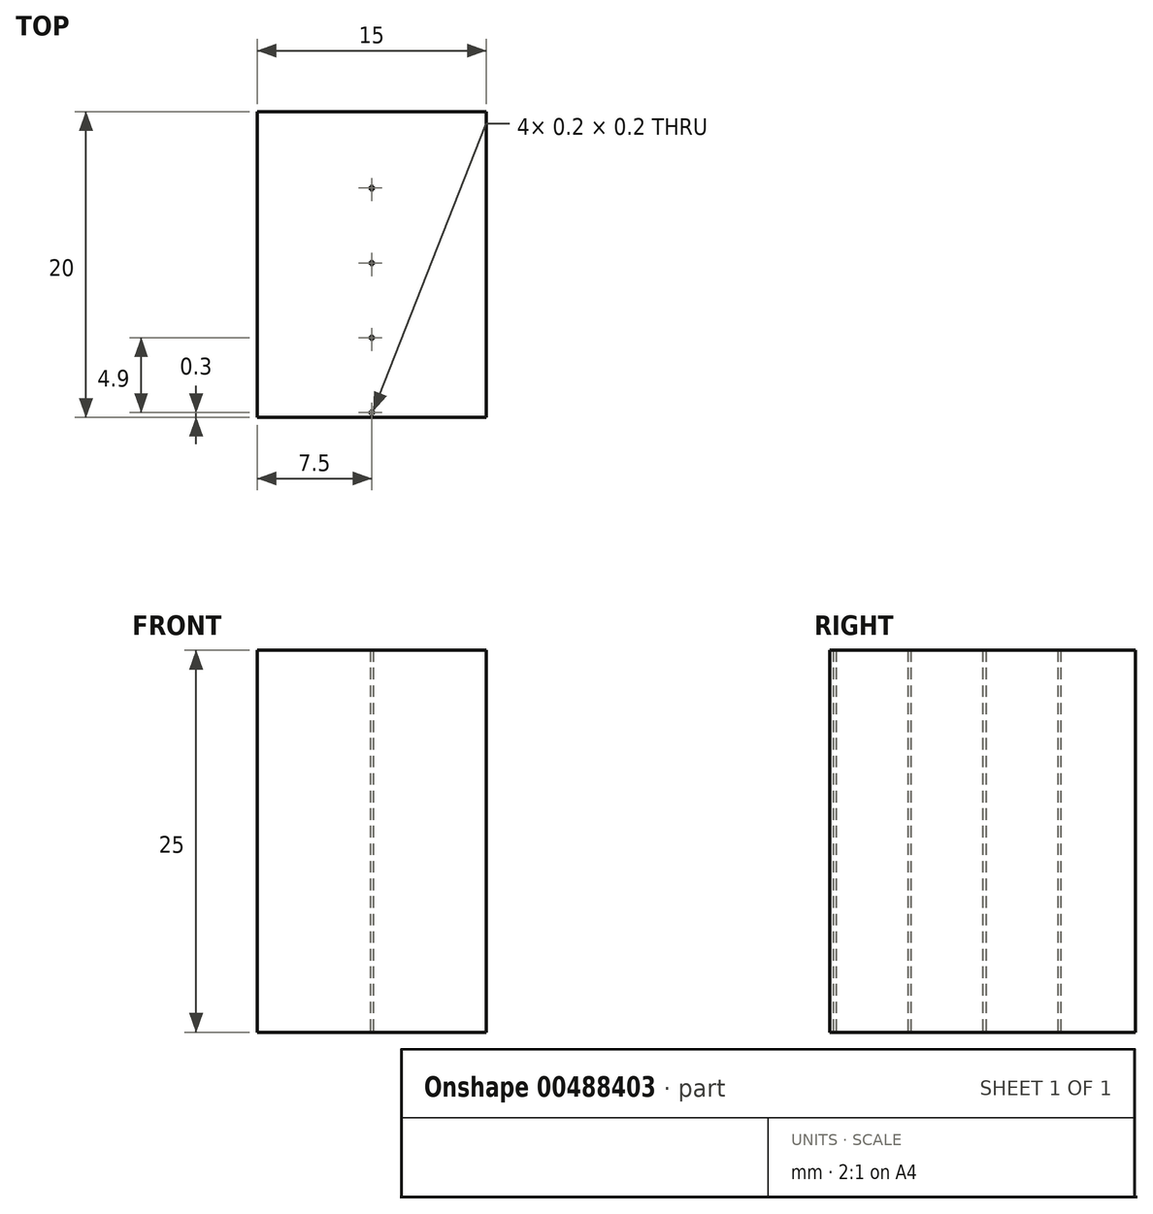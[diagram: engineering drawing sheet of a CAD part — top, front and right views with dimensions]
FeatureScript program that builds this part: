
annotation { "Feature Type Name" : "Feature", "Feature Type Description" : "" }
export const myFeature = defineFeature(function(context is Context, id is Id, definition is map)
    precondition{}
    {
        {
            var Q0;
            Q0=qCreatedBy(makeId("Top.planeOp"),FACE);
            var sketch = newSketch(context, id + "F0", { "sketchPlane" : qUnion([Q0])});
            skLineSegment(sketch, "E0.bottom", {"start": v(-7.5, 10) * mm, "end": v(7.5, 10) * mm});
            skLineSegment(sketch, "E0.top", {"start": v(-7.5, -10) * mm, "end": v(7.5, -10) * mm});
            skLineSegment(sketch, "E0.left", {"start": v(-7.5, 10) * mm, "end": v(-7.5, -10) * mm});
            skLineSegment(sketch, "E0.right", {"start": v(7.5, 10) * mm, "end": v(7.5, -10) * mm});
            skPoint(sketch, "E0.middle", {"position": v(0, 0) * mm});
            skLineSegment(sketch, "E1.bottom", {"start": v(-7.5, 10) * mm, "end": v(-7.3, 10) * mm});
            skLineSegment(sketch, "E1.top", {"start": v(-7.5, 9.8) * mm, "end": v(-7.3, 9.8) * mm});
            skLineSegment(sketch, "E1.left", {"start": v(-7.5, 10) * mm, "end": v(-7.5, 9.8) * mm});
            skLineSegment(sketch, "E1.right", {"start": v(-7.3, 10) * mm, "end": v(-7.3, 9.8) * mm});
            skLineSegment(sketch, "E2.0.1.0", {"start": v(-7.5, 4.9) * mm, "end": v(-7.3, 4.9) * mm});
            skLineSegment(sketch, "E2.0.1.1", {"start": v(-7.5, 5.1) * mm, "end": v(-7.3, 5.1) * mm});
            skLineSegment(sketch, "E2.0.1.2", {"start": v(-7.3, 5.1) * mm, "end": v(-7.3, 4.9) * mm});
            skLineSegment(sketch, "E2.0.1.3", {"start": v(-7.5, 5.1) * mm, "end": v(-7.5, 4.9) * mm});
            skLineSegment(sketch, "E2.0.2.0", {"start": v(-7.5, 0) * mm, "end": v(-7.3, 0) * mm});
            skLineSegment(sketch, "E2.0.2.1", {"start": v(-7.5, 0.2) * mm, "end": v(-7.3, 0.2) * mm});
            skLineSegment(sketch, "E2.0.2.2", {"start": v(-7.3, 0.2) * mm, "end": v(-7.3, 0) * mm});
            skLineSegment(sketch, "E2.0.2.3", {"start": v(-7.5, 0.2) * mm, "end": v(-7.5, 0) * mm});
            skLineSegment(sketch, "E2.0.3.0", {"start": v(-7.5, -4.9) * mm, "end": v(-7.3, -4.9) * mm});
            skLineSegment(sketch, "E2.0.3.1", {"start": v(-7.5, -4.7) * mm, "end": v(-7.3, -4.7) * mm});
            skLineSegment(sketch, "E2.0.3.2", {"start": v(-7.3, -4.7) * mm, "end": v(-7.3, -4.9) * mm});
            skLineSegment(sketch, "E2.0.3.3", {"start": v(-7.5, -4.7) * mm, "end": v(-7.5, -4.9) * mm});
            skLineSegment(sketch, "E2.0.4.0", {"start": v(-7.5, -9.8) * mm, "end": v(-7.3, -9.8) * mm});
            skLineSegment(sketch, "E2.0.4.1", {"start": v(-7.5, -9.6) * mm, "end": v(-7.3, -9.6) * mm});
            skLineSegment(sketch, "E2.0.4.2", {"start": v(-7.3, -9.6) * mm, "end": v(-7.3, -9.8) * mm});
            skLineSegment(sketch, "E2.0.4.3", {"start": v(-7.5, -9.6) * mm, "end": v(-7.5, -9.8) * mm});
            skLineSegment(sketch, "E2.1.0.0", {"start": v(-0.1, 9.8) * mm, "end": v(0.1, 9.8) * mm});
            skLineSegment(sketch, "E2.1.0.1", {"start": v(-0.1, 10) * mm, "end": v(0.1, 10) * mm});
            skLineSegment(sketch, "E2.1.0.2", {"start": v(0.1, 10) * mm, "end": v(0.1, 9.8) * mm});
            skLineSegment(sketch, "E2.1.0.3", {"start": v(-0.1, 10) * mm, "end": v(-0.1, 9.8) * mm});
            skLineSegment(sketch, "E2.1.1.0", {"start": v(-0.1, 4.9) * mm, "end": v(0.1, 4.9) * mm});
            skLineSegment(sketch, "E2.1.1.1", {"start": v(-0.1, 5.1) * mm, "end": v(0.1, 5.1) * mm});
            skLineSegment(sketch, "E2.1.1.2", {"start": v(0.1, 5.1) * mm, "end": v(0.1, 4.9) * mm});
            skLineSegment(sketch, "E2.1.1.3", {"start": v(-0.1, 5.1) * mm, "end": v(-0.1, 4.9) * mm});
            skLineSegment(sketch, "E2.1.2.0", {"start": v(-0.1, 0) * mm, "end": v(0.1, 0) * mm});
            skLineSegment(sketch, "E2.1.2.1", {"start": v(-0.1, 0.2) * mm, "end": v(0.1, 0.2) * mm});
            skLineSegment(sketch, "E2.1.2.2", {"start": v(0.1, 0.2) * mm, "end": v(0.1, 0) * mm});
            skLineSegment(sketch, "E2.1.2.3", {"start": v(-0.1, 0.2) * mm, "end": v(-0.1, 0) * mm});
            skLineSegment(sketch, "E2.1.3.0", {"start": v(-0.1, -4.9) * mm, "end": v(0.1, -4.9) * mm});
            skLineSegment(sketch, "E2.1.3.1", {"start": v(-0.1, -4.7) * mm, "end": v(0.1, -4.7) * mm});
            skLineSegment(sketch, "E2.1.3.2", {"start": v(0.1, -4.7) * mm, "end": v(0.1, -4.9) * mm});
            skLineSegment(sketch, "E2.1.3.3", {"start": v(-0.1, -4.7) * mm, "end": v(-0.1, -4.9) * mm});
            skLineSegment(sketch, "E2.1.4.0", {"start": v(-0.1, -9.8) * mm, "end": v(0.1, -9.8) * mm});
            skLineSegment(sketch, "E2.1.4.1", {"start": v(-0.1, -9.6) * mm, "end": v(0.1, -9.6) * mm});
            skLineSegment(sketch, "E2.1.4.2", {"start": v(0.1, -9.6) * mm, "end": v(0.1, -9.8) * mm});
            skLineSegment(sketch, "E2.1.4.3", {"start": v(-0.1, -9.6) * mm, "end": v(-0.1, -9.8) * mm});
            skLineSegment(sketch, "E2.2.0.0", {"start": v(7.3, 9.8) * mm, "end": v(7.5, 9.8) * mm});
            skLineSegment(sketch, "E2.2.0.1", {"start": v(7.3, 10) * mm, "end": v(7.5, 10) * mm});
            skLineSegment(sketch, "E2.2.0.2", {"start": v(7.5, 10) * mm, "end": v(7.5, 9.8) * mm});
            skLineSegment(sketch, "E2.2.0.3", {"start": v(7.3, 10) * mm, "end": v(7.3, 9.8) * mm});
            skLineSegment(sketch, "E2.2.1.0", {"start": v(7.3, 4.9) * mm, "end": v(7.5, 4.9) * mm});
            skLineSegment(sketch, "E2.2.1.1", {"start": v(7.3, 5.1) * mm, "end": v(7.5, 5.1) * mm});
            skLineSegment(sketch, "E2.2.1.2", {"start": v(7.5, 5.1) * mm, "end": v(7.5, 4.9) * mm});
            skLineSegment(sketch, "E2.2.1.3", {"start": v(7.3, 5.1) * mm, "end": v(7.3, 4.9) * mm});
            skLineSegment(sketch, "E2.2.2.0", {"start": v(7.3, 0) * mm, "end": v(7.5, 0) * mm});
            skLineSegment(sketch, "E2.2.2.1", {"start": v(7.3, 0.2) * mm, "end": v(7.5, 0.2) * mm});
            skLineSegment(sketch, "E2.2.2.2", {"start": v(7.5, 0.2) * mm, "end": v(7.5, 0) * mm});
            skLineSegment(sketch, "E2.2.2.3", {"start": v(7.3, 0.2) * mm, "end": v(7.3, 0) * mm});
            skLineSegment(sketch, "E2.2.3.0", {"start": v(7.3, -4.9) * mm, "end": v(7.5, -4.9) * mm});
            skLineSegment(sketch, "E2.2.3.1", {"start": v(7.3, -4.7) * mm, "end": v(7.5, -4.7) * mm});
            skLineSegment(sketch, "E2.2.3.2", {"start": v(7.5, -4.7) * mm, "end": v(7.5, -4.9) * mm});
            skLineSegment(sketch, "E2.2.3.3", {"start": v(7.3, -4.7) * mm, "end": v(7.3, -4.9) * mm});
            skLineSegment(sketch, "E2.2.4.0", {"start": v(7.3, -9.8) * mm, "end": v(7.5, -9.8) * mm});
            skLineSegment(sketch, "E2.2.4.1", {"start": v(7.3, -9.6) * mm, "end": v(7.5, -9.6) * mm});
            skLineSegment(sketch, "E2.2.4.2", {"start": v(7.5, -9.6) * mm, "end": v(7.5, -9.8) * mm});
            skLineSegment(sketch, "E2.2.4.3", {"start": v(7.3, -9.6) * mm, "end": v(7.3, -9.8) * mm});
            skLineSegment(sketch, "E2.direction1", {"start": v(-7.5, 9.8) * mm, "end": v(-0.1, 9.8) * mm, "construction": true});
            skLineSegment(sketch, "E2.direction2", {"start": v(-7.5, 9.8) * mm, "end": v(-7.5, 4.9) * mm, "construction": true});
            skSolve(sketch);
        }
        {
            var Q0;
            {var subQ13=sQuery(id+"F0.wireOp",EDGE,"E0.top");Q0=makeQuery(id+"F0.imprint","IMPRINT",FACE,{"disambiguationData":[TD([[makeQuery(id+"F0.imprint","IMPRINT",EDGE,{"derivedFrom":subQ13}),1.0]])]});}
            extrude(context, id + "F1", {"entities" : qUnion([Q0]), "depth" : 0.72 * mm});
        }
        {
            var Q0;
            Q0 = qSketchRegion(id + "F0", true);
            extrude(context, id + "F2", {"entities" : qUnion([Q0]), "operationType" : NewBodyOperationType.ADD, "depth" : 25 * mm});
        }
    });
